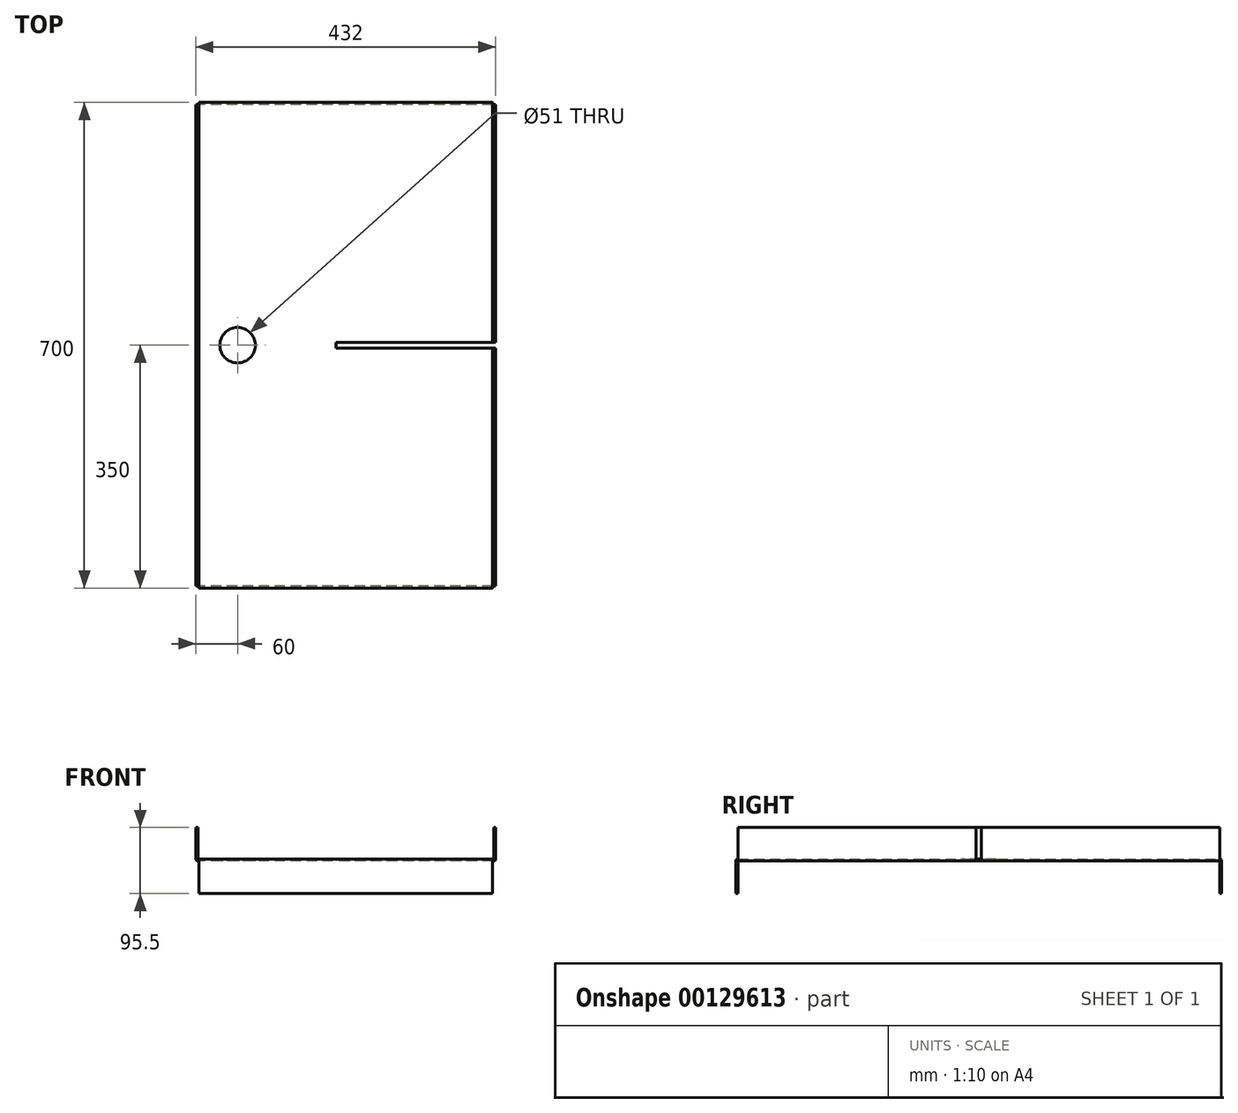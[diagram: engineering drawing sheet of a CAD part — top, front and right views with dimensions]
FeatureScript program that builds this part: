
annotation { "Feature Type Name" : "Feature", "Feature Type Description" : "" }
export const myFeature = defineFeature(function(context is Context, id is Id, definition is map)
    precondition{}
    {
        {
            var Q0;
            Q0=qCreatedBy(makeId("Right.planeOp"),FACE);
            var sketch = newSketch(context, id + "F0", { "sketchPlane" : qUnion([Q0])});
            skLineSegment(sketch, "E0", {"start": v(-350, 1.5) * mm, "end": v(-350, -45.5) * mm});
            skLineSegment(sketch, "E1", {"start": v(-345.5, 1.5) * mm, "end": v(345.5, 1.5) * mm});
            skLineSegment(sketch, "E2", {"start": v(350, -45.5) * mm, "end": v(350, 1.5) * mm});
            skLineSegment(sketch, "E3", {"start": v(-350, -45.5) * mm, "end": v(350, -45.5) * mm, "construction": true});
            skLineSegment(sketch, "E4", {"start": v(-350, -45.5) * mm, "end": v(-347, -45.5) * mm});
            skLineSegment(sketch, "E5", {"start": v(-347, 0) * mm, "end": v(-347, -45.5) * mm});
            skLineSegment(sketch, "E6", {"start": v(-347, 4.5) * mm, "end": v(347, 4.5) * mm});
            skLineSegment(sketch, "E7", {"start": v(347, -45.5) * mm, "end": v(347, 0) * mm});
            skLineSegment(sketch, "E8", {"start": v(347, -45.5) * mm, "end": v(350, -45.5) * mm});
            skPoint(sketch, "E9.visualSharp", {"position": v(-347, 1.5) * mm});
            skArc(sketch, "E9.filletArc", {"start": v(-345.5, 1.5) * mm, "mid": v(-346.56, 1.06) * mm, "end": v(-347, 0) * mm});
            skPoint(sketch, "E10.visualSharp", {"position": v(-350, 4.5) * mm});
            skArc(sketch, "E10.filletArc", {"start": v(-347, 4.5) * mm, "mid": v(-349.12, 3.62) * mm, "end": v(-350, 1.5) * mm});
            skPoint(sketch, "E11.visualSharp", {"position": v(350, 4.5) * mm});
            skArc(sketch, "E11.filletArc", {"start": v(350, 1.5) * mm, "mid": v(349.12, 3.62) * mm, "end": v(347, 4.5) * mm});
            skArc(sketch, "E12.filletArc", {"start": v(347, 0) * mm, "mid": v(346.56, 1.06) * mm, "end": v(345.5, 1.5) * mm});
            skSolve(sketch);
        }
        {
            var Q0;
            Q0=qSketchRegion(id+"F0",true);
            extrude(context, id + "F1", {"entities" : qUnion([Q0]), "depth" : 211.5 * mm, "hasSecondDirection" : true, "secondDirectionOppositeDirection" : true, "secondDirectionDepth" : 70 * mm});
        }
        {
            var Q0;
            Q0=qCreatedBy(makeId("Front.planeOp"),FACE);
            var sketch = newSketch(context, id + "F2", { "sketchPlane" : qUnion([Q0])});
            skLineSegment(sketch, "E13", {"start": v(213, 50) * mm, "end": v(216, 50) * mm});
            skLineSegment(sketch, "E14", {"start": v(216, 50) * mm, "end": v(216, 4.5) * mm});
            skLineSegment(sketch, "E15", {"start": v(213, 50) * mm, "end": v(213, 4.5) * mm});
            skArc(sketch, "E16.filletArc", {"start": v(211.5, 3) * mm, "mid": v(212.56, 3.44) * mm, "end": v(213, 4.5) * mm});
            skPoint(sketch, "E17.visualSharp", {"position": v(216, 0) * mm});
            skArc(sketch, "E17.filletArc", {"start": v(213, 1.5) * mm, "mid": v(215.12, 2.38) * mm, "end": v(216, 4.5) * mm});
            skLineSegment(sketch, "E18", {"start": v(211.5, 3) * mm, "end": v(211.5, 1.5) * mm});
            skLineSegment(sketch, "E19", {"start": v(213, 1.5) * mm, "end": v(211.5, 1.5) * mm});
            skSolve(sketch);
        }
        {
            var Q0;
            Q0=qSketchRegion(id+"F2",true);
            extrude(context, id + "F3", {"entities" : qUnion([Q0]), "operationType" : NewBodyOperationType.ADD, "depth" : 347 * mm, "hasSecondDirection" : true, "secondDirectionOppositeDirection" : true, "secondDirectionDepth" : 347 * mm});
        }
        {
            var Q0;
            Q0=makeQuery(id+"F1.opExtrude","SWEPT_BODY",BODY,{"disambiguationData":[OSD([sQuery(id+"F0.wireOp",EDGE,"E0"),sQuery(id+"F0.wireOp",EDGE,"E1"),sQuery(id+"F0.wireOp",EDGE,"E2"),sQuery(id+"F0.wireOp",EDGE,"E4"),sQuery(id+"F0.wireOp",EDGE,"E5"),sQuery(id+"F0.wireOp",EDGE,"E6"),sQuery(id+"F0.wireOp",EDGE,"E7"),sQuery(id+"F0.wireOp",EDGE,"E8"),sQuery(id+"F0.wireOp",EDGE,"E9.filletArc"),sQuery(id+"F0.wireOp",EDGE,"E10.filletArc"),sQuery(id+"F0.wireOp",EDGE,"E11.filletArc"),sQuery(id+"F0.wireOp",EDGE,"E12.filletArc")])]});
            var Q1;
            Q1=qCreatedBy(makeId("Right.planeOp"),FACE);
            mirror(context, id + "F4", {"operationType" : NewBodyOperationType.ADD, "entities" : qUnion([Q0]), "mirrorPlane" : qUnion([Q1])});
        }
        {
            var Q0;
            Q0=qCreatedBy(makeId("Top.planeOp"),FACE);
            var sketch = newSketch(context, id + "F5", { "sketchPlane" : qUnion([Q0])});
            skLineSegment(sketch, "E20.bottom", {"start": v(-14, -4) * mm, "end": v(219.84, -4) * mm});
            skLineSegment(sketch, "E20.top", {"start": v(-14, 4) * mm, "end": v(219.84, 4) * mm});
            skLineSegment(sketch, "E20.left", {"start": v(-14, -4) * mm, "end": v(-14, 4) * mm});
            skLineSegment(sketch, "E20.right", {"start": v(219.84, -4) * mm, "end": v(219.84, 4) * mm});
            skSolve(sketch);
        }
        {
            var Q0;
            Q0=makeQuery(id+"F5.imprint","IMPRINT",FACE,{"disambiguationData":[TD([[makeQuery(id+"F5.imprint","IMPRINT",EDGE,{"derivedFrom":sQuery(id+"F5.wireOp",EDGE,"E20.bottom")}),1.0]])]});
            extrude(context, id + "F6", {"entities" : qUnion([Q0]), "operationType" : NewBodyOperationType.REMOVE, "depth" : 80 * mm});
        }
        {
            var Q0;
            {var subQ0=makeQuery(id+"F3.boolean.opBoolean","MERGE",FACE,{"derivedFrom":[makeQuery(id+"F1.opExtrude","SWEPT_FACE",FACE,{"disambiguationData":[OSD([sQuery(id+"F0.wireOp",EDGE,"E1")])]}),makeQuery(id+"F3.opExtrude","SWEPT_FACE",FACE,{"disambiguationData":[OSD([sQuery(id+"F2.wireOp",EDGE,"E19")])]})]});Q0=makeQuery(id+"F4.boolean.opBoolean","MERGE",FACE,{"derivedFrom":[subQ0,makeQuery(id+"F4.opPattern","COPY",FACE,{"derivedFrom":subQ0,"instanceName":"1"})]});}
            var sketch = newSketch(context, id + "F7", { "sketchPlane" : qUnion([Q0])});
            skCircle(sketch, "E21", {"center": v(-156, 0) * mm, "radius": 25.5 * mm});
            skSolve(sketch);
        }
        {
            var Q0;
            Q0=qSketchRegion(id+"F7",true);
            extrude(context, id + "F8", {"entities" : qUnion([Q0]), "operationType" : NewBodyOperationType.REMOVE, "endBound" : BoundingType.SYMMETRIC, "oppositeDirection" : true, "depth" : 25 * mm});
        }
    });
